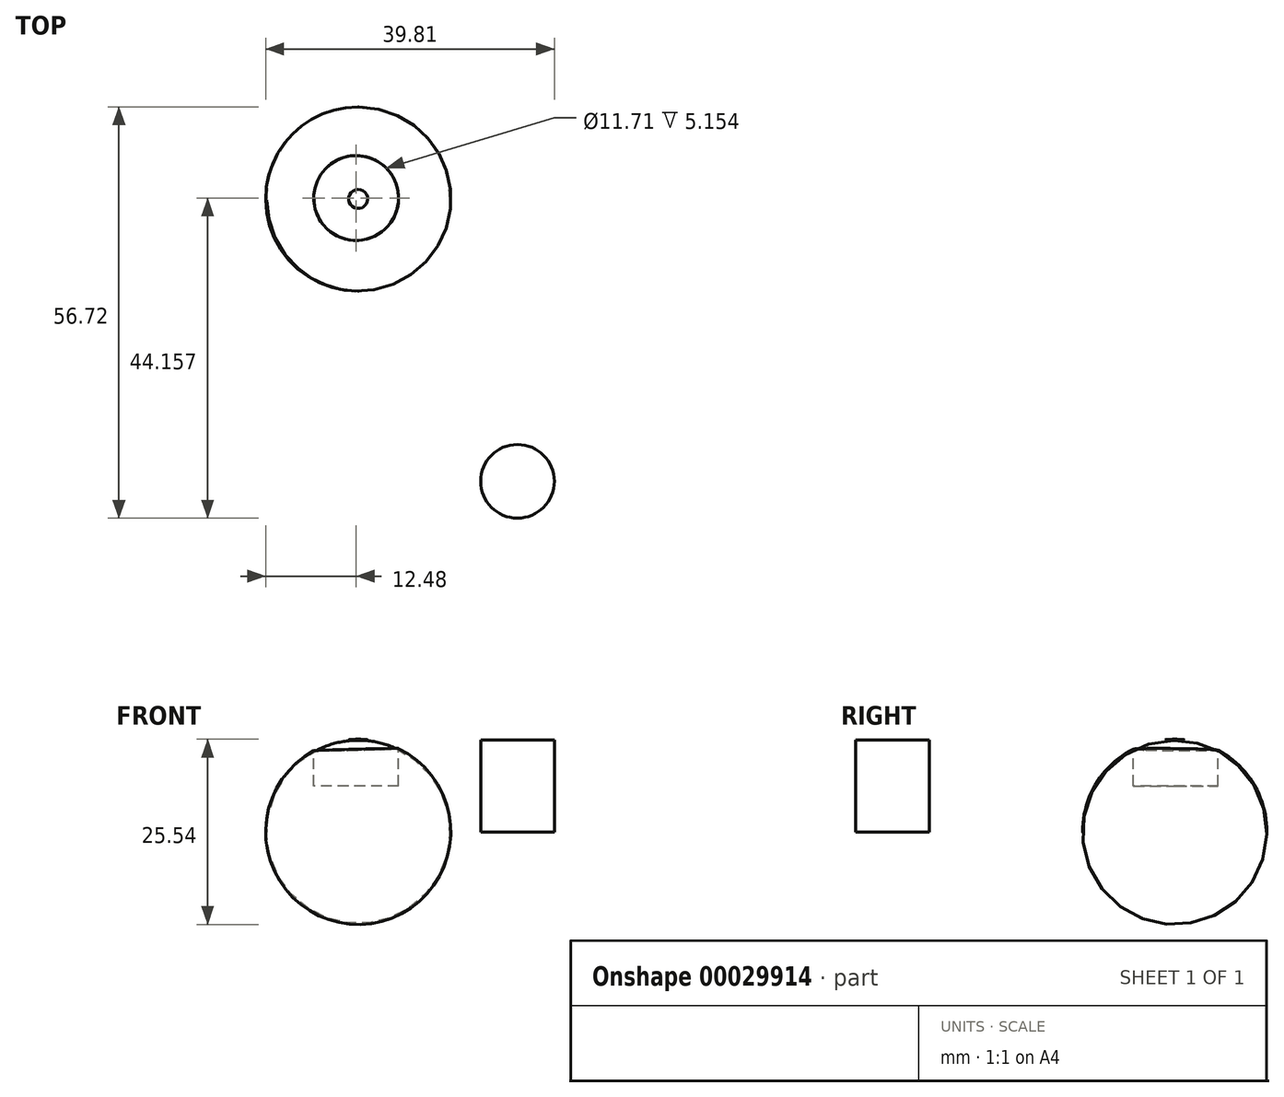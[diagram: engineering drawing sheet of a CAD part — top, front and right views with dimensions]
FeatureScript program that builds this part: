
annotation { "Feature Type Name" : "Feature", "Feature Type Description" : "" }
export const myFeature = defineFeature(function(context is Context, id is Id, definition is map)
    precondition{}
    {
        {
            var Q0;
            Q0=qCreatedBy(makeId("Top.planeOp"),FACE);
            var sketch = newSketch(context, id + "F0", { "sketchPlane" : qUnion([Q0])});
            skCircle(sketch, "E0", {"center": v(-22.4, -4.42) * mm, "radius": 5.08 * mm});
            skLineSegment(sketch, "E1", {"start": v(-44.35, 47.22) * mm, "end": v(-44.35, 21.82) * mm});
            skArc(sketch, "E2", {"start": v(-44.35, 21.82) * mm, "mid": v(-31.59, 34.52) * mm, "end": v(-44.35, 47.22) * mm});
            skSolve(sketch);
        }
        {
            var Q0;
            Q0=makeQuery(id+"F0.imprint","IMPRINT",FACE,{"disambiguationData":[TD([[makeQuery(id+"F0.imprint","IMPRINT",EDGE,{"derivedFrom":sQuery(id+"F0.wireOp",EDGE,"E0")}),1.0]])]});
            extrude(context, id + "F1", {"entities" : qUnion([Q0]), "depth" : 12.7 * mm});
        }
        {
            var Q0;
            Q0=makeQuery(id+"F0.imprint","IMPRINT",FACE,{"disambiguationData":[TD([[makeQuery(id+"F0.imprint","IMPRINT",EDGE,{"derivedFrom":sQuery(id+"F0.wireOp",EDGE,"E1")}),1.0]])]});
            var Q1;
            Q1=sQuery(id+"F0.wireOp",EDGE,"E1");
            revolve(context, id + "F2", {"entities" : qUnion([Q0]), "axis" : qUnion([Q1]), "revolveType" : RevolveType.FULL});
        }
        {
            var Q0;
            Q0=qCreatedBy(makeId("Top.planeOp"),FACE);
            cPlane(context, id + "F3", {"entities" : qUnion([Q0]), "cplaneType" : CPlaneType.OFFSET, "offset" : 12.7 * mm, "width" : 152.4 * mm, "height" : 152.4 * mm});
        }
        {
            var Q0;
            Q0=qCreatedBy(id+"F3.planeOp",FACE);
            var sketch = newSketch(context, id + "F4", { "sketchPlane" : qUnion([Q0])});
            skCircle(sketch, "E3", {"center": v(-44.64, 34.66) * mm, "radius": 5.85 * mm});
            skSolve(sketch);
        }
        {
            var Q0;
            Q0=makeQuery(id+"F4.imprint","IMPRINT",FACE,{"disambiguationData":[TD([[makeQuery(id+"F4.imprint","IMPRINT",EDGE,{"derivedFrom":sQuery(id+"F4.wireOp",EDGE,"E3")}),1.0]])]});
            extrude(context, id + "F5", {"entities" : qUnion([Q0]), "operationType" : NewBodyOperationType.REMOVE, "oppositeDirection" : true, "depth" : 6.35 * mm});
        }
    });
